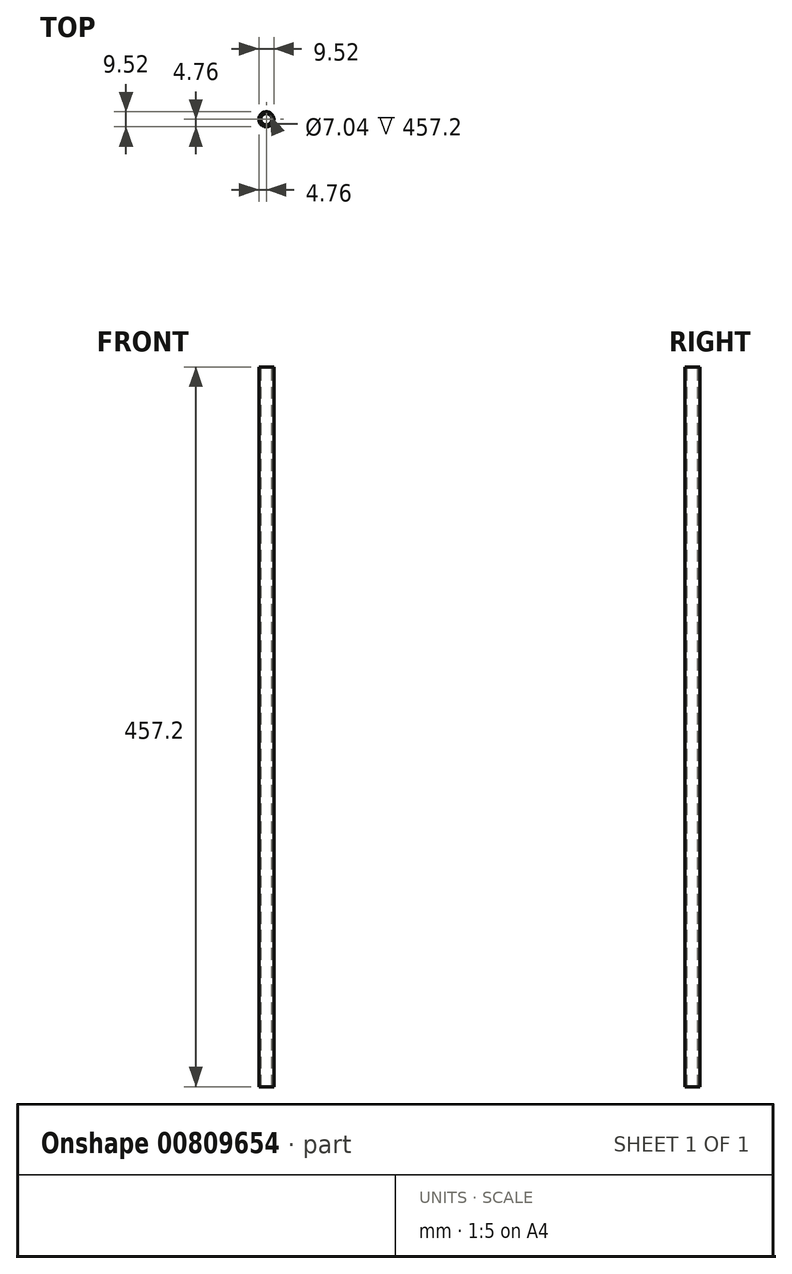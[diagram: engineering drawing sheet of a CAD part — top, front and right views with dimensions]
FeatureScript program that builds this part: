
annotation { "Feature Type Name" : "Feature", "Feature Type Description" : "" }
export const myFeature = defineFeature(function(context is Context, id is Id, definition is map)
    precondition{}
    {
        {
            var Q0;
            Q0=qCreatedBy(makeId("Top.planeOp"),FACE);
            var sketch = newSketch(context, id + "F0", { "sketchPlane" : qUnion([Q0])});
            skCircle(sketch, "E0", {"center": v(0, -304.8) * mm, "radius": 4.76 * mm});
            skCircle(sketch, "E1", {"center": v(0, -304.8) * mm, "radius": 3.52 * mm});
            skSolve(sketch);
        }
        {
            var Q0;
            Q0=makeQuery(id+"F0.imprint","IMPRINT",FACE,{"disambiguationData":[TD([[makeQuery(id+"F0.imprint","IMPRINT",EDGE,{"derivedFrom":sQuery(id+"F0.wireOp",EDGE,"E0")}),1.0]])]});
            extrude(context, id + "F1", {"entities" : qUnion([Q0]), "oppositeDirection" : true, "depth" : 457.2 * mm, "offsetDistance" : 25.4 * mm});
        }
    });
